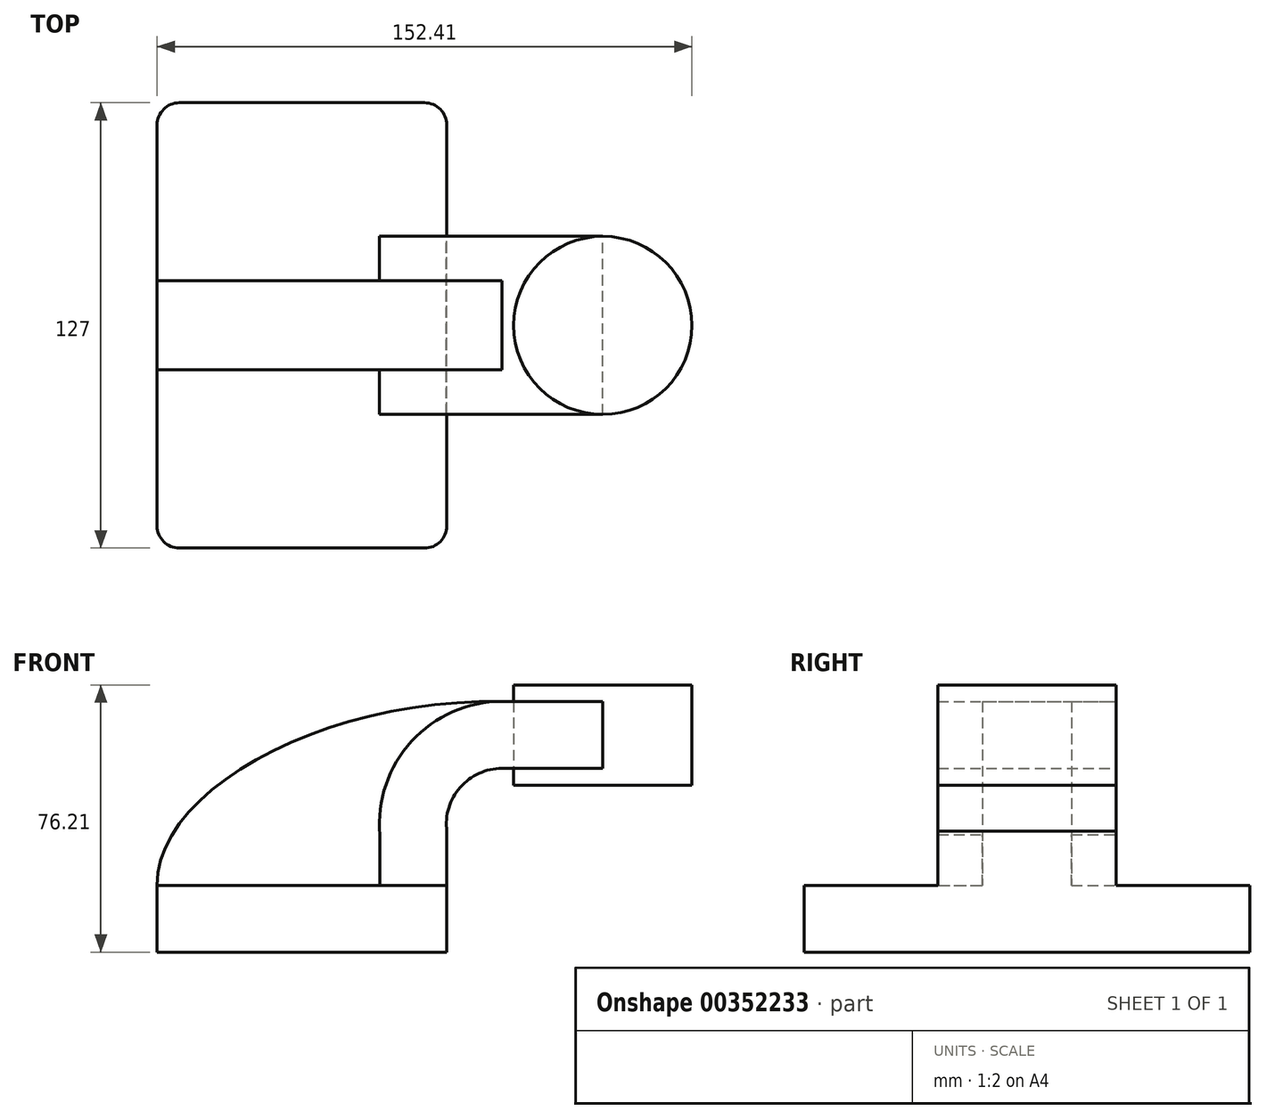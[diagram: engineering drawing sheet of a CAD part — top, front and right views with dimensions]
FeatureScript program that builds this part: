
annotation { "Feature Type Name" : "Feature", "Feature Type Description" : "" }
export const myFeature = defineFeature(function(context is Context, id is Id, definition is map)
    precondition{}
    {
        {
            var Q0;
            Q0=qCreatedBy(makeId("Front.planeOp"),FACE);
            var sketch = newSketch(context, id + "F0", { "sketchPlane" : qUnion([Q0])});
            skLineSegment(sketch, "E0.bottom", {"start": v(-41.28, -9.53) * mm, "end": v(41.28, -9.53) * mm});
            skLineSegment(sketch, "E0.top", {"start": v(-41.28, 9.53) * mm, "end": v(41.28, 9.53) * mm});
            skLineSegment(sketch, "E0.left", {"start": v(-41.28, -9.53) * mm, "end": v(-41.28, 9.53) * mm});
            skLineSegment(sketch, "E0.right", {"start": v(41.28, -9.53) * mm, "end": v(41.28, 9.53) * mm});
            skPoint(sketch, "E0.middle", {"position": v(0, 0) * mm});
            skLineSegment(sketch, "E1.bottom", {"start": v(111.12, 38.1) * mm, "end": v(60.32, 38.1) * mm});
            skLineSegment(sketch, "E1.top", {"start": v(111.12, 66.68) * mm, "end": v(60.32, 66.68) * mm});
            skLineSegment(sketch, "E1.left", {"start": v(111.12, 38.1) * mm, "end": v(111.12, 66.68) * mm});
            skLineSegment(sketch, "E1.right", {"start": v(60.32, 38.1) * mm, "end": v(60.32, 66.68) * mm});
            skPoint(sketch, "E1.middle", {"position": v(85.72, 52.39) * mm});
            skLineSegment(sketch, "E2", {"start": v(41.28, 9.52) * mm, "end": v(41.28, 24.93) * mm});
            skLineSegment(sketch, "E3", {"start": v(57.01, 42.88) * mm, "end": v(85.72, 42.88) * mm});
            skArc(sketch, "E4", {"start": v(57.01, 42.88) * mm, "mid": v(45.08, 37.47) * mm, "end": v(41.27, 24.93) * mm});
            skLineSegment(sketch, "E5.0", {"start": v(57.01, 61.93) * mm, "end": v(85.72, 61.93) * mm});
            skArc(sketch, "E5.1", {"start": v(57.01, 61.93) * mm, "mid": v(31.25, 50.58) * mm, "end": v(22.22, 23.92) * mm});
            skLineSegment(sketch, "E5.2", {"start": v(22.22, 9.52) * mm, "end": v(22.22, 23.92) * mm});
            skLineSegment(sketch, "E6", {"start": v(85.72, 38.1) * mm, "end": v(85.72, 66.68) * mm});
            skFitSpline(sketch, "E7", {"points": [v(57.01, 61.93) * mm, v(-41.28, 9.53) * mm], "startDerivative": vector(-148.27, 3) * mm, "endDerivative": vector(0.57, -83.73) * mm});
            skSolve(sketch);
        }
        {
            var Q0;
            Q0=makeQuery(id+"F0.imprint","IMPRINT",FACE,{"disambiguationData":[TD([[makeQuery(id+"F0.imprint","IMPRINT",EDGE,{"derivedFrom":sQuery(id+"F0.wireOp",EDGE,"E0.bottom")}),1.0]])]});
            extrude(context, id + "F1", {"entities" : qUnion([Q0]), "endBound" : BoundingType.SYMMETRIC, "depth" : 127 * mm});
        }
        {
            var Q0;
            {var subQ4=sQuery(id+"F0.wireOp",EDGE,"E2");Q0=makeQuery(id+"F0.imprint","IMPRINT",FACE,{"disambiguationData":[TD([[makeQuery(id+"F0.imprint","IMPRINT",EDGE,{"derivedFrom":subQ4}),1.0]])]});}
            var Q1;
            {var subQ0=sQuery(id+"F0.wireOp",EDGE,"E3");var subQ1=sQuery(id+"F0.wireOp",EDGE,"E1.right");var subQ2=makeQuery(id+"F0.imprint","INTERSECT",VERTEX,{"derivedFrom":[subQ1,subQ0]});Q1=makeQuery(id+"F0.imprint","IMPRINT",FACE,{"disambiguationData":[TD([[makeQuery(id+"F0.imprint","IMPRINT",EDGE,{"disambiguationData":[TD([[subQ2,-1.0]])],"derivedFrom":subQ1}),-1.0]])]});}
            extrude(context, id + "F2", {"entities" : qUnion([Q0, Q1]), "operationType" : NewBodyOperationType.ADD, "endBound" : BoundingType.SYMMETRIC, "depth" : 50.8 * mm});
        }
        {
            var Q0;
            Q0=makeQuery(id+"F0.imprint","IMPRINT",FACE,{"disambiguationData":[TD([[makeQuery(id+"F0.imprint","IMPRINT",EDGE,{"derivedFrom":sQuery(id+"F0.wireOp",EDGE,"E5.1")}),-1.0]])]});
            var Q1;
            Q1 = qSketchRegion(id + "FQS9TZ8MHEKMbe5_1", true);
            extrude(context, id + "F3", {"entities" : qUnion([Q0, Q1]), "operationType" : NewBodyOperationType.ADD, "endBound" : BoundingType.SYMMETRIC, "depth" : 25.4 * mm});
        }
        {
            var Q0;
            {var subQ4=sQuery(id+"F0.wireOp",EDGE,"E1.left");Q0=makeQuery(id+"F0.imprint","IMPRINT",FACE,{"disambiguationData":[TD([[makeQuery(id+"F0.imprint","IMPRINT",EDGE,{"derivedFrom":subQ4}),1.0]])]});}
            var Q1;
            Q1=sQuery(id+"F0.wireOp",EDGE,"E6");
            revolve(context, id + "F4", {"entities" : qUnion([Q0]), "axis" : qUnion([Q1]), "revolveType" : RevolveType.FULL});
        }
        {
            var Q0;
            Q0=makeQuery(id+"F1.opExtrude","CAP_EDGE",EDGE,{"disambiguationData":[OSD([sQuery(id+"F0.wireOp",EDGE,"E0.right")])],"isStart":false});
            var Q1;
            Q1=makeQuery(id+"F1.opExtrude","CAP_EDGE",EDGE,{"disambiguationData":[OSD([sQuery(id+"F0.wireOp",EDGE,"E0.left")])],"isStart":false});
            var Q2;
            Q2=makeQuery(id+"F1.opExtrude","CAP_EDGE",EDGE,{"disambiguationData":[OSD([sQuery(id+"F0.wireOp",EDGE,"E0.left")])],"isStart":true});
            var Q3;
            Q3=makeQuery(id+"F1.opExtrude","CAP_EDGE",EDGE,{"disambiguationData":[OSD([sQuery(id+"F0.wireOp",EDGE,"E0.right")])],"isStart":true});
            fillet(context, id + "F5", {"entities" : qUnion([Q0, Q1, Q2, Q3]), "radius" : 6.35 * mm, "tangentPropagation" : true, "allowEdgeOverflow" : false});
        }
    });
